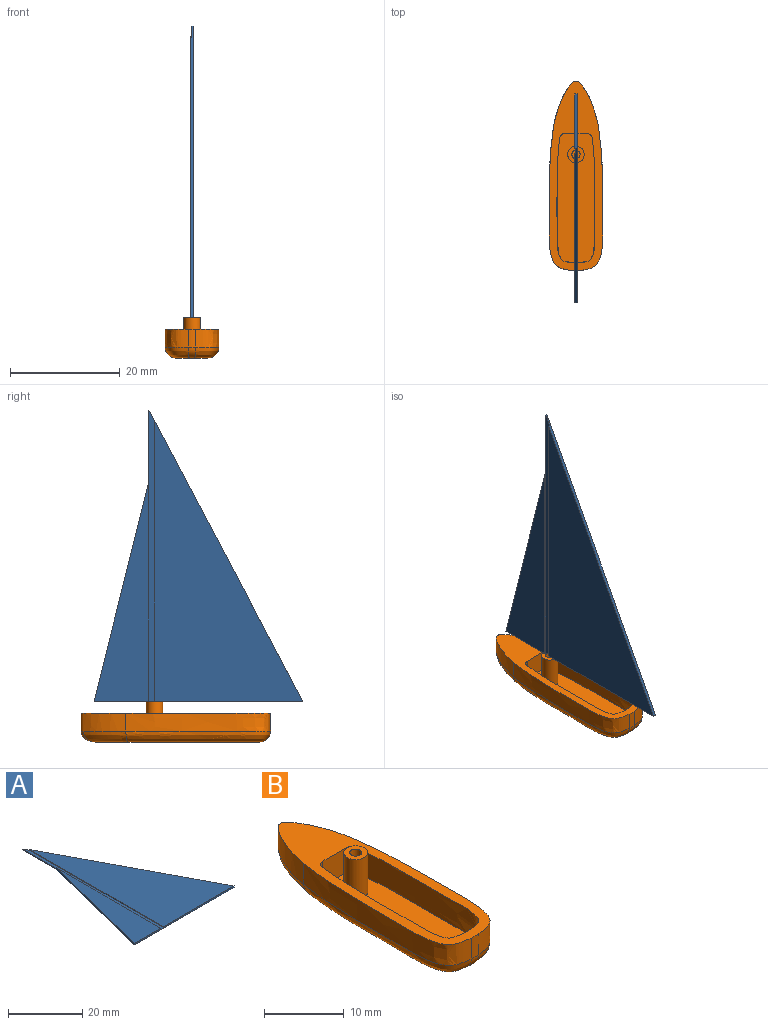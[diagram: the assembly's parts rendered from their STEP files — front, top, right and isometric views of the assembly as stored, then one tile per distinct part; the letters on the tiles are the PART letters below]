
ASSEMBLY  parts=2 mates=1
PART A: 10 faces, bbox 38x53x0.5 mm
  f0: plane 13x0.26mm, normal (-1,0,0), area 3.4mm2, adj f1,f4,f6,f9
  f1: plane 53x28mm, normal (0.88,0.47,0), area 30.9mm2, adj f0,f3,f5,f6,f8,f9
  f2: plane 40x10mm, normal (0,0,1), area 200mm2, adj f4,f5,f7
  f3: plane 51.11x27mm, normal (0,0,1), area 689.9mm2, adj f1,f5,f8
  f4: plane 40x10mm, normal (-0.97,0.24,0), area 21.6mm2, adj f0,f2,f5,f6,f7
  f5: plane 38x0.53mm, normal (0,-1,0), area 19.7mm2, adj f1,f2,f3,f4,f6,f7,f8,f9
  f6: plane 53x38mm, normal (0,0,-1), area 942mm2, adj f0,f1,f4,f5
  f7: plane 40x0.26mm, normal (1,0,0), area 10.5mm2, adj f2,f4,f5,f9
  f8: plane 51.11x0.26mm, normal (-1,0,0), area 13.4mm2, adj f1,f3,f5,f9
  f9: plane 53x1mm, normal (0,0,1), area 52.1mm2, adj f0,f1,f5,f7,f8
PART B: 24 faces, bbox 10.4x35.2x7.4 mm
  f0: plane 29.83x5.83mm, normal (0,0,-1), area 144.9mm2, adj f10,f11,f12,f13,f21
  f1: plane 34.56x10.43mm, normal (0,0,1), area 131.7mm2, adj f2,f3,f4,f5,f6,f8,f9,f18
  f2: extruded ~26.3x4.22mm, area 92.1mm2, adj f1,f9,f10,f20
  f3: extruded ~26.3x4.22mm, area 92.1mm2, adj f1,f8,f11,f20
  f4: extruded ~22.7x3.8mm, area 95.1mm2, adj f1,f5,f7,f23
  f5: extruded ~22.7x3.8mm, area 95.1mm2, adj f1,f4,f7,f22
  f6: plane 4.02x3.8mm, normal (0,-1,0), area 15.3mm2, adj f1,f7,f22,f23
  f7: plane 23.58x7.03mm, normal (0,0,1), area 148.8mm2, adj f4,f5,f6,f15,f22,f23
  f8: extruded ~7.77x3.29mm, area 27.3mm2, adj f1,f3,f13,f18
  f9: extruded ~7.77x3.29mm, area 27.3mm2, adj f1,f2,f12,f18
  f10: bspline ~32.13x5.02mm, area 86.5mm2, adj f0,f2,f12,f21
  f11: bspline ~32.13x5.02mm, area 86.5mm2, adj f0,f3,f13,f21
  f12: bspline ~11.25x5.76mm, area 23.6mm2, adj f0,f9,f10,f19
  f13: bspline ~11.25x5.76mm, area 23.6mm2, adj f0,f8,f11,f19
  f14: cylinder r=0.75mm len=6mm, axis (0,0,-1), area 28.3mm2, adj f16,f17
  f15: cylinder r=1.5mm len=6mm, axis (0,0,-1), area 56.5mm2, adj f7,f16
  f16: plane 3x3mm, normal (0,0,1), area 5.3mm2, adj f14,f15
  f17: plane 1.5x1.5mm, normal (0,0,1), area 1.8mm2, adj f14
  f18: cylinder r=1mm len=3.2mm, axis (0,0,-1), area 5.7mm2, adj f1,f8,f9,f19
  f19: bspline ~3.26x2.31mm, area 2.8mm2, adj f12,f13,f18
  f20: cylinder r=6mm len=3.2mm, axis (0,0,-1), area 4.4mm2, adj f1,f2,f3,f21
  f21: torus R=4mm, axis (0,0,1), area 3.8mm2, adj f0,f10,f11,f20
  f22: cylinder r=1mm len=3.8mm, axis (0,0,-1), area 5.5mm2, adj f1,f5,f6,f7
  f23: cylinder r=1mm len=3.8mm, axis (0,0,-1), area 5.5mm2, adj f1,f4,f6,f7
PLACE A rot(axis=(0.58,-0.58,-0.58),120deg) t=(0.19,-4.04,7.96)mm
PLACE B t=(-0.07,-13.04,0.56)mm
MATE fastened A.f5 <-> B.f14  axis (0,0,-1) through (-0.07,-5.04,7.96)mm
